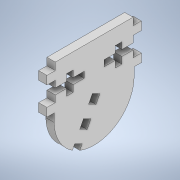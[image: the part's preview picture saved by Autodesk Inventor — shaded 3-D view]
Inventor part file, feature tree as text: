
AUTODESK INVENTOR PART (.ipt)
format: ipt  version: 2020 (Build 240168000, 168)  size: 194,560 bytes
history: native  units: mm
features: other x6, extrude x1, sketch x1
ambient origin geometry x8: Origin, YZ Plane, XZ Plane, XY Plane, X Axis, Y Axis, Z Axis, Center Point
bodies: Solide1 (feature_tree)
feature tree (8):
  other  "Table"
  other  "top_axis"
  other  "Blocs"
  extrude  "Extrusion1"  Depth=1.5mm TaperAngle=0.0deg
  sketch  "Esquisse1"
  other  "Half"
  other  "Half:1"
  other  "Half:2"
